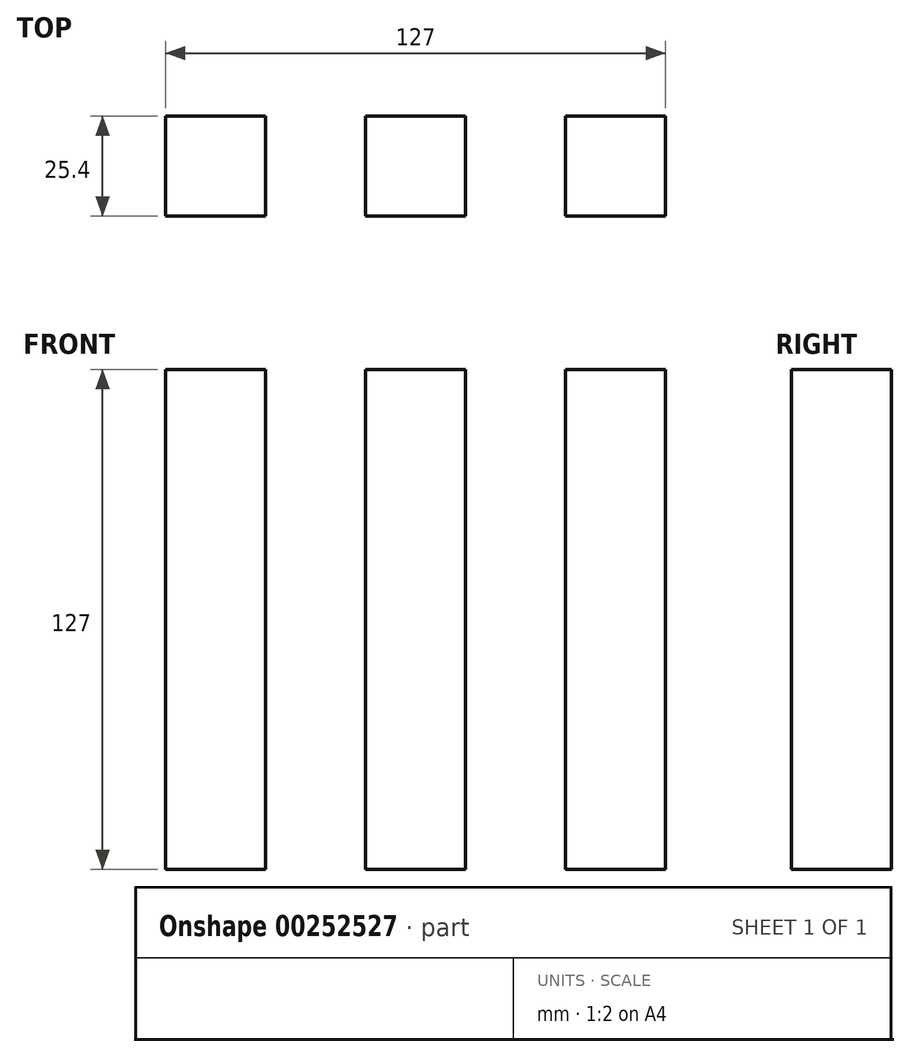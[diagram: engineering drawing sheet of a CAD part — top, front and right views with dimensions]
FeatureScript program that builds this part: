
annotation { "Feature Type Name" : "Feature", "Feature Type Description" : "" }
export const myFeature = defineFeature(function(context is Context, id is Id, definition is map)
    precondition{}
    {
        {
            var Q0;
            Q0=qCreatedBy(makeId("Front.planeOp"),FACE);
            var sketch = newSketch(context, id + "F0", { "sketchPlane" : qUnion([Q0])});
            skLineSegment(sketch, "E0.bottom", {"start": v(12.7, 63.5) * mm, "end": v(-12.7, 63.5) * mm});
            skLineSegment(sketch, "E0.top", {"start": v(12.7, -63.5) * mm, "end": v(-12.7, -63.5) * mm});
            skLineSegment(sketch, "E0.left", {"start": v(12.7, 63.5) * mm, "end": v(12.7, -63.5) * mm});
            skLineSegment(sketch, "E0.right", {"start": v(-12.7, 63.5) * mm, "end": v(-12.7, -63.5) * mm});
            skPoint(sketch, "E0.middle", {"position": v(0, 0) * mm});
            skLineSegment(sketch, "E1.bottom", {"start": v(63.5, 63.5) * mm, "end": v(38.1, 63.5) * mm});
            skLineSegment(sketch, "E1.top", {"start": v(63.5, -63.5) * mm, "end": v(38.1, -63.5) * mm});
            skLineSegment(sketch, "E1.left", {"start": v(63.5, 63.5) * mm, "end": v(63.5, -63.5) * mm});
            skLineSegment(sketch, "E1.right", {"start": v(38.1, 63.5) * mm, "end": v(38.1, -63.5) * mm});
            skPoint(sketch, "E1.middle", {"position": v(50.8, 0) * mm});
            skLineSegment(sketch, "E2.bottom", {"start": v(-63.5, 63.5) * mm, "end": v(-38.1, 63.5) * mm});
            skLineSegment(sketch, "E2.top", {"start": v(-63.5, -63.5) * mm, "end": v(-38.1, -63.5) * mm});
            skLineSegment(sketch, "E2.left", {"start": v(-63.5, 63.5) * mm, "end": v(-63.5, -63.5) * mm});
            skLineSegment(sketch, "E2.right", {"start": v(-38.1, 63.5) * mm, "end": v(-38.1, -63.5) * mm});
            skPoint(sketch, "E2.middle", {"position": v(-50.8, 0) * mm});
            skSolve(sketch);
        }
        {
            var Q0;
            Q0 = qSketchRegion(id + "F0", true);
            extrude(context, id + "F1", {"entities" : qUnion([Q0]), "endBound" : BoundingType.SYMMETRIC, "depth" : 25.4 * mm});
        }
    });
